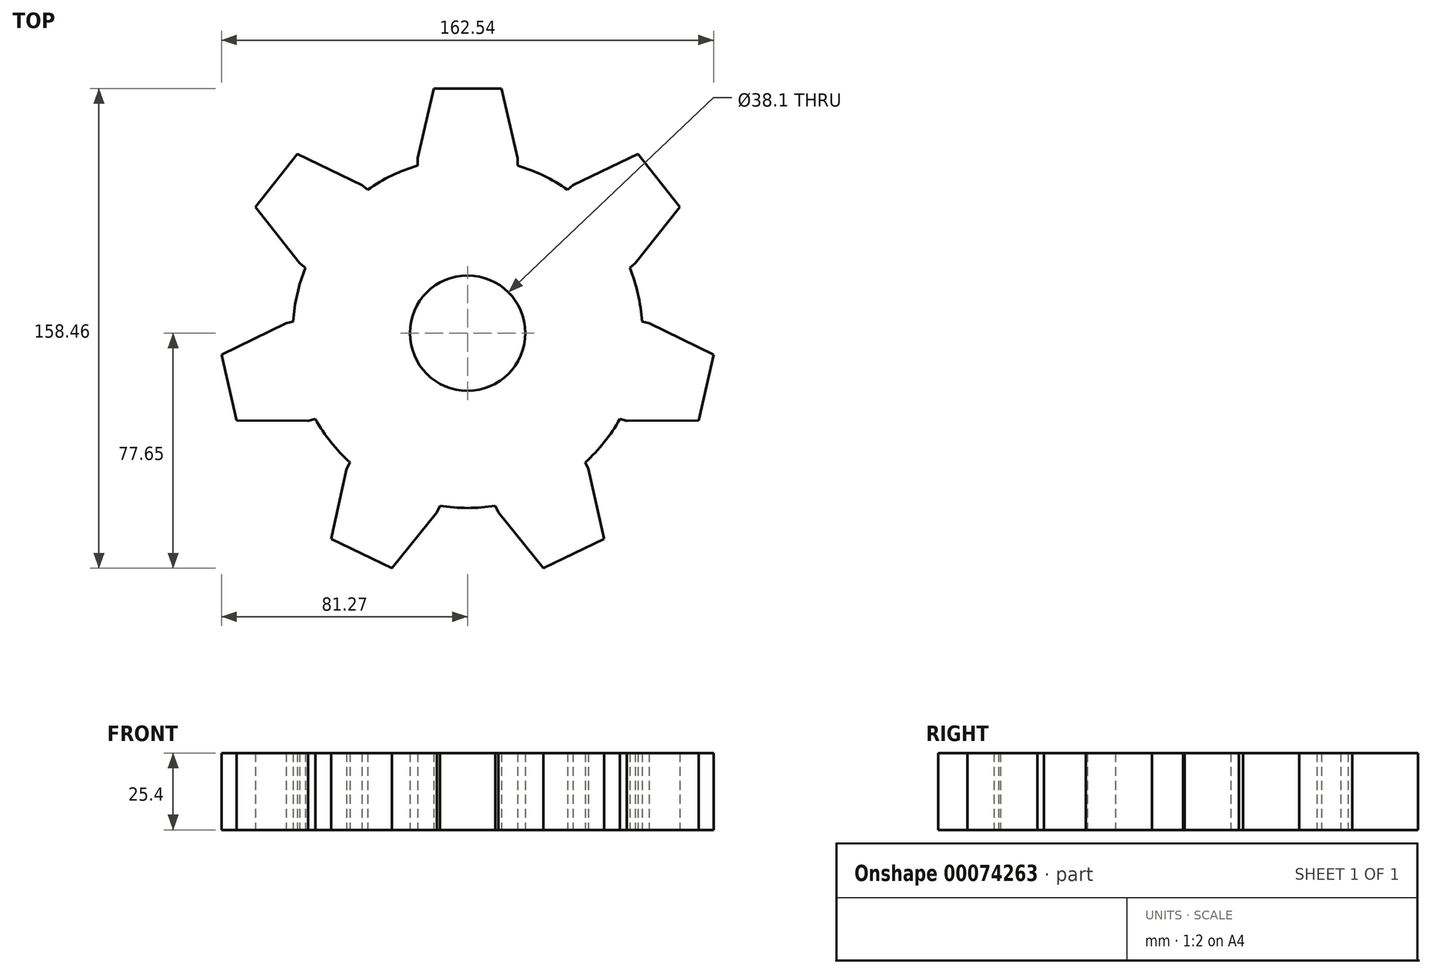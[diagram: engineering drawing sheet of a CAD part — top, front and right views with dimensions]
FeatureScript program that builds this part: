
annotation { "Feature Type Name" : "Feature", "Feature Type Description" : "" }
export const myFeature = defineFeature(function(context is Context, id is Id, definition is map)
    precondition{}
    {
        {
            var Q0;
            Q0=qCreatedBy(makeId("Top.planeOp"),FACE);
            var sketch = newSketch(context, id + "F0", { "sketchPlane" : qUnion([Q0])});
            skCircle(sketch, "E0", {"center": v(0, 0) * mm, "radius": 57.75 * mm});
            skLineSegment(sketch, "E1", {"start": v(0, 64.12) * mm, "end": v(0, -63.7) * mm, "construction": true});
            skLineSegment(sketch, "E2", {"start": v(-16.5, 57.75) * mm, "end": v(16.5, 57.75) * mm, "construction": true});
            skPoint(sketch, "E3", {"position": v(0, 57.75) * mm});
            skLineSegment(sketch, "E4", {"start": v(-16.49, 55.35) * mm, "end": v(-16.51, 57.75) * mm});
            skLineSegment(sketch, "E5", {"start": v(-16.5, 57.75) * mm, "end": v(-11.16, 80.81) * mm});
            skLineSegment(sketch, "E6", {"start": v(-11.16, 80.81) * mm, "end": v(0, 80.81) * mm});
            skLineSegment(sketch, "E7", {"start": v(0, 80.81) * mm, "end": v(0, 57.75) * mm});
            skLineSegment(sketch, "E8.MirrorCS", {"start": v(11.16, 80.81) * mm, "end": v(0, 80.81) * mm});
            skLineSegment(sketch, "E9.MirrorCS", {"start": v(16.5, 57.75) * mm, "end": v(11.16, 80.81) * mm});
            skLineSegment(sketch, "E10.MirrorCS", {"start": v(16.49, 55.35) * mm, "end": v(16.51, 57.75) * mm});
            skLineSegment(sketch, "E11.1.0", {"start": v(-53.55, 21.62) * mm, "end": v(-55.45, 23.1) * mm});
            skLineSegment(sketch, "E11.1.1", {"start": v(-55.45, 23.1) * mm, "end": v(-70.14, 41.66) * mm});
            skLineSegment(sketch, "E11.1.2", {"start": v(-70.14, 41.66) * mm, "end": v(-63.18, 50.38) * mm});
            skLineSegment(sketch, "E11.1.3", {"start": v(-56.22, 59.1) * mm, "end": v(-63.18, 50.38) * mm});
            skLineSegment(sketch, "E11.1.4", {"start": v(-34.86, 48.92) * mm, "end": v(-56.22, 59.1) * mm});
            skLineSegment(sketch, "E11.1.5", {"start": v(-33, 47.4) * mm, "end": v(-34.86, 48.92) * mm});
            skLineSegment(sketch, "E11.2.0", {"start": v(-50.3, -28.4) * mm, "end": v(-52.63, -28.95) * mm});
            skLineSegment(sketch, "E11.2.1", {"start": v(-52.63, -28.95) * mm, "end": v(-76.3, -28.86) * mm});
            skLineSegment(sketch, "E11.2.2", {"start": v(-76.3, -28.86) * mm, "end": v(-78.78, -17.98) * mm});
            skLineSegment(sketch, "E11.2.3", {"start": v(-81.27, -7.1) * mm, "end": v(-78.78, -17.98) * mm});
            skLineSegment(sketch, "E11.2.4", {"start": v(-59.98, 3.24) * mm, "end": v(-81.27, -7.1) * mm});
            skLineSegment(sketch, "E11.2.5", {"start": v(-57.63, 3.76) * mm, "end": v(-59.98, 3.24) * mm});
            skLineSegment(sketch, "E11.3.0", {"start": v(-9.16, -57.02) * mm, "end": v(-10.18, -59.2) * mm});
            skLineSegment(sketch, "E11.3.1", {"start": v(-10.18, -59.2) * mm, "end": v(-25, -77.65) * mm});
            skLineSegment(sketch, "E11.3.2", {"start": v(-25, -77.65) * mm, "end": v(-35.06, -72.8) * mm});
            skLineSegment(sketch, "E11.3.3", {"start": v(-45.12, -67.97) * mm, "end": v(-35.06, -72.8) * mm});
            skLineSegment(sketch, "E11.3.4", {"start": v(-39.93, -44.87) * mm, "end": v(-45.12, -67.97) * mm});
            skLineSegment(sketch, "E11.3.5", {"start": v(-38.87, -42.71) * mm, "end": v(-39.93, -44.87) * mm});
            skLineSegment(sketch, "E11.4.0", {"start": v(38.87, -42.71) * mm, "end": v(39.93, -44.87) * mm});
            skLineSegment(sketch, "E11.4.1", {"start": v(39.93, -44.87) * mm, "end": v(45.12, -67.97) * mm});
            skLineSegment(sketch, "E11.4.2", {"start": v(45.12, -67.97) * mm, "end": v(35.06, -72.8) * mm});
            skLineSegment(sketch, "E11.4.3", {"start": v(25, -77.65) * mm, "end": v(35.06, -72.8) * mm});
            skLineSegment(sketch, "E11.4.4", {"start": v(10.18, -59.2) * mm, "end": v(25, -77.65) * mm});
            skLineSegment(sketch, "E11.4.5", {"start": v(9.16, -57.02) * mm, "end": v(10.18, -59.2) * mm});
            skLineSegment(sketch, "E11.5.0", {"start": v(57.63, 3.76) * mm, "end": v(59.98, 3.24) * mm});
            skLineSegment(sketch, "E11.5.1", {"start": v(59.98, 3.24) * mm, "end": v(81.27, -7.1) * mm});
            skLineSegment(sketch, "E11.5.2", {"start": v(81.27, -7.1) * mm, "end": v(78.78, -17.98) * mm});
            skLineSegment(sketch, "E11.5.3", {"start": v(76.3, -28.86) * mm, "end": v(78.78, -17.98) * mm});
            skLineSegment(sketch, "E11.5.4", {"start": v(52.63, -28.95) * mm, "end": v(76.3, -28.86) * mm});
            skLineSegment(sketch, "E11.5.5", {"start": v(50.3, -28.4) * mm, "end": v(52.63, -28.95) * mm});
            skLineSegment(sketch, "E11.6.0", {"start": v(33, 47.4) * mm, "end": v(34.86, 48.92) * mm});
            skLineSegment(sketch, "E11.6.1", {"start": v(34.86, 48.92) * mm, "end": v(56.22, 59.1) * mm});
            skLineSegment(sketch, "E11.6.2", {"start": v(56.22, 59.1) * mm, "end": v(63.18, 50.38) * mm});
            skLineSegment(sketch, "E11.6.3", {"start": v(70.14, 41.66) * mm, "end": v(63.18, 50.38) * mm});
            skLineSegment(sketch, "E11.6.4", {"start": v(55.45, 23.1) * mm, "end": v(70.14, 41.66) * mm});
            skLineSegment(sketch, "E11.6.5", {"start": v(53.55, 21.62) * mm, "end": v(55.45, 23.1) * mm});
            skCircle(sketch, "E12", {"center": v(0, 0) * mm, "radius": 19.05 * mm});
            skSolve(sketch);
        }
        {
            var Q0;
            {var subQ0=sQuery(id+"F0.wireOp",EDGE,"E11.3.0");Q0=makeQuery(id+"F0.imprint","IMPRINT",FACE,{"disambiguationData":[TD([[makeQuery(id+"F0.imprint","IMPRINT",EDGE,{"derivedFrom":subQ0}),-1.0]])]});}
            var Q1;
            {var subQ1=sQuery(id+"F0.wireOp",EDGE,"E11.2.0");Q1=makeQuery(id+"F0.imprint","IMPRINT",FACE,{"disambiguationData":[TD([[makeQuery(id+"F0.imprint","IMPRINT",EDGE,{"derivedFrom":subQ1}),-1.0]])]});}
            var Q2;
            {var subQ0=sQuery(id+"F0.wireOp",EDGE,"E11.1.0");Q2=makeQuery(id+"F0.imprint","IMPRINT",FACE,{"disambiguationData":[TD([[makeQuery(id+"F0.imprint","IMPRINT",EDGE,{"derivedFrom":subQ0}),-1.0]])]});}
            var Q3;
            {var subQ0=sQuery(id+"F0.wireOp",EDGE,"E11.6.0");Q3=makeQuery(id+"F0.imprint","IMPRINT",FACE,{"disambiguationData":[TD([[makeQuery(id+"F0.imprint","IMPRINT",EDGE,{"derivedFrom":subQ0}),-1.0]])]});}
            var Q4;
            {var subQ0=sQuery(id+"F0.wireOp",EDGE,"E7");Q4=makeQuery(id+"F0.imprint","IMPRINT",FACE,{"disambiguationData":[TD([[makeQuery(id+"F0.imprint","IMPRINT",EDGE,{"derivedFrom":subQ0}),1.0]])]});}
            var Q5;
            {var subQ0=sQuery(id+"F0.wireOp",EDGE,"E4");Q5=makeQuery(id+"F0.imprint","IMPRINT",FACE,{"disambiguationData":[TD([[makeQuery(id+"F0.imprint","IMPRINT",EDGE,{"derivedFrom":subQ0}),-1.0]])]});}
            var Q6;
            {var subQ0=sQuery(id+"F0.wireOp",EDGE,"E11.5.0");Q6=makeQuery(id+"F0.imprint","IMPRINT",FACE,{"disambiguationData":[TD([[makeQuery(id+"F0.imprint","IMPRINT",EDGE,{"derivedFrom":subQ0}),-1.0]])]});}
            var Q7;
            {var subQ0=sQuery(id+"F0.wireOp",EDGE,"E11.4.0");Q7=makeQuery(id+"F0.imprint","IMPRINT",FACE,{"disambiguationData":[TD([[makeQuery(id+"F0.imprint","IMPRINT",EDGE,{"derivedFrom":subQ0}),-1.0]])]});}
            var Q8;
            Q8=makeQuery(id+"F0.imprint","IMPRINT",FACE,{"disambiguationData":[TD([[makeQuery(id+"F0.imprint","IMPRINT",EDGE,{"derivedFrom":sQuery(id+"F0.wireOp",EDGE,"E12")}),-1.0]])]});
            extrude(context, id + "F1", {"entities" : qUnion([Q0, Q1, Q2, Q3, Q4, Q5, Q6, Q7, Q8]), "depth" : 25.4 * mm});
        }
    });
